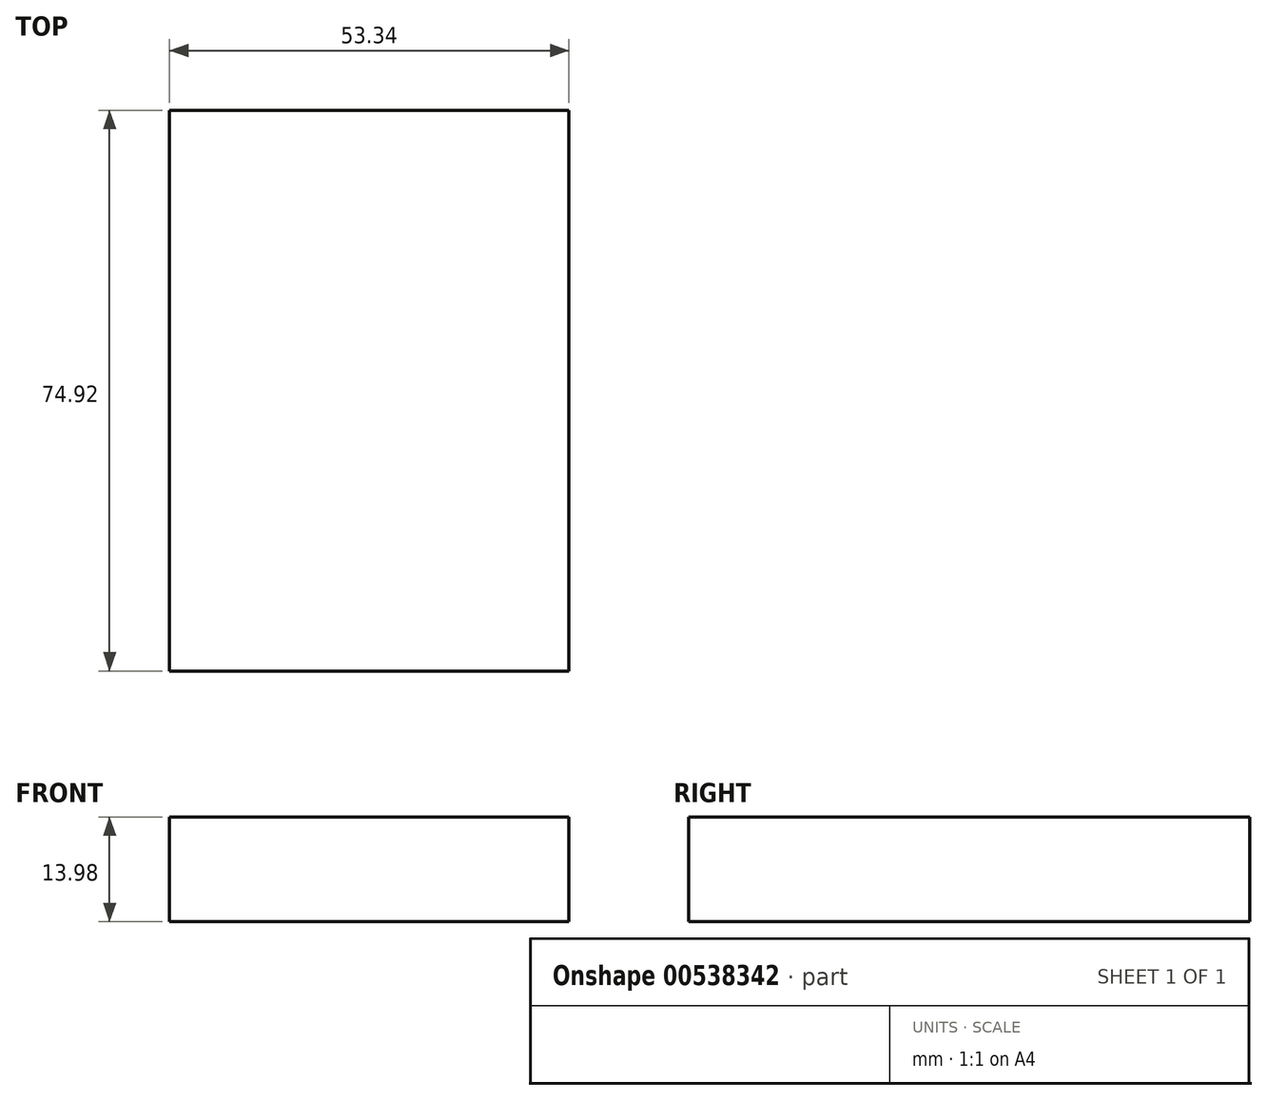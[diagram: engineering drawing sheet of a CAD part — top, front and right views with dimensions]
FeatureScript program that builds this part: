
annotation { "Feature Type Name" : "Feature", "Feature Type Description" : "" }
export const myFeature = defineFeature(function(context is Context, id is Id, definition is map)
    precondition{}
    {
        {
            var Q0;
            Q0=qCreatedBy(makeId("Front.planeOp"),FACE);
            var sketch = newSketch(context, id + "F0", { "sketchPlane" : qUnion([Q0])});
            skLineSegment(sketch, "E0.bottom", {"start": v(26.67, 6.99) * mm, "end": v(-26.67, 6.99) * mm});
            skLineSegment(sketch, "E0.top", {"start": v(26.67, -6.99) * mm, "end": v(-26.67, -6.99) * mm});
            skLineSegment(sketch, "E0.left", {"start": v(26.67, 6.99) * mm, "end": v(26.67, -6.99) * mm});
            skLineSegment(sketch, "E0.right", {"start": v(-26.67, 6.99) * mm, "end": v(-26.67, -6.99) * mm});
            skPoint(sketch, "E0.middle", {"position": v(0, 0) * mm});
            skSolve(sketch);
        }
        {
            var Q0;
            Q0=makeQuery(id+"F0.imprint","IMPRINT",FACE,{"disambiguationData":[TD([[makeQuery(id+"F0.imprint","IMPRINT",EDGE,{"derivedFrom":sQuery(id+"F0.wireOp",EDGE,"E0.bottom")}),1.0]])]});
            extrude(context, id + "F1", {"entities" : qUnion([Q0]), "endBound" : BoundingType.SYMMETRIC, "depth" : 74.93 * mm, "offsetDistance" : 25.4 * mm});
        }
    });
